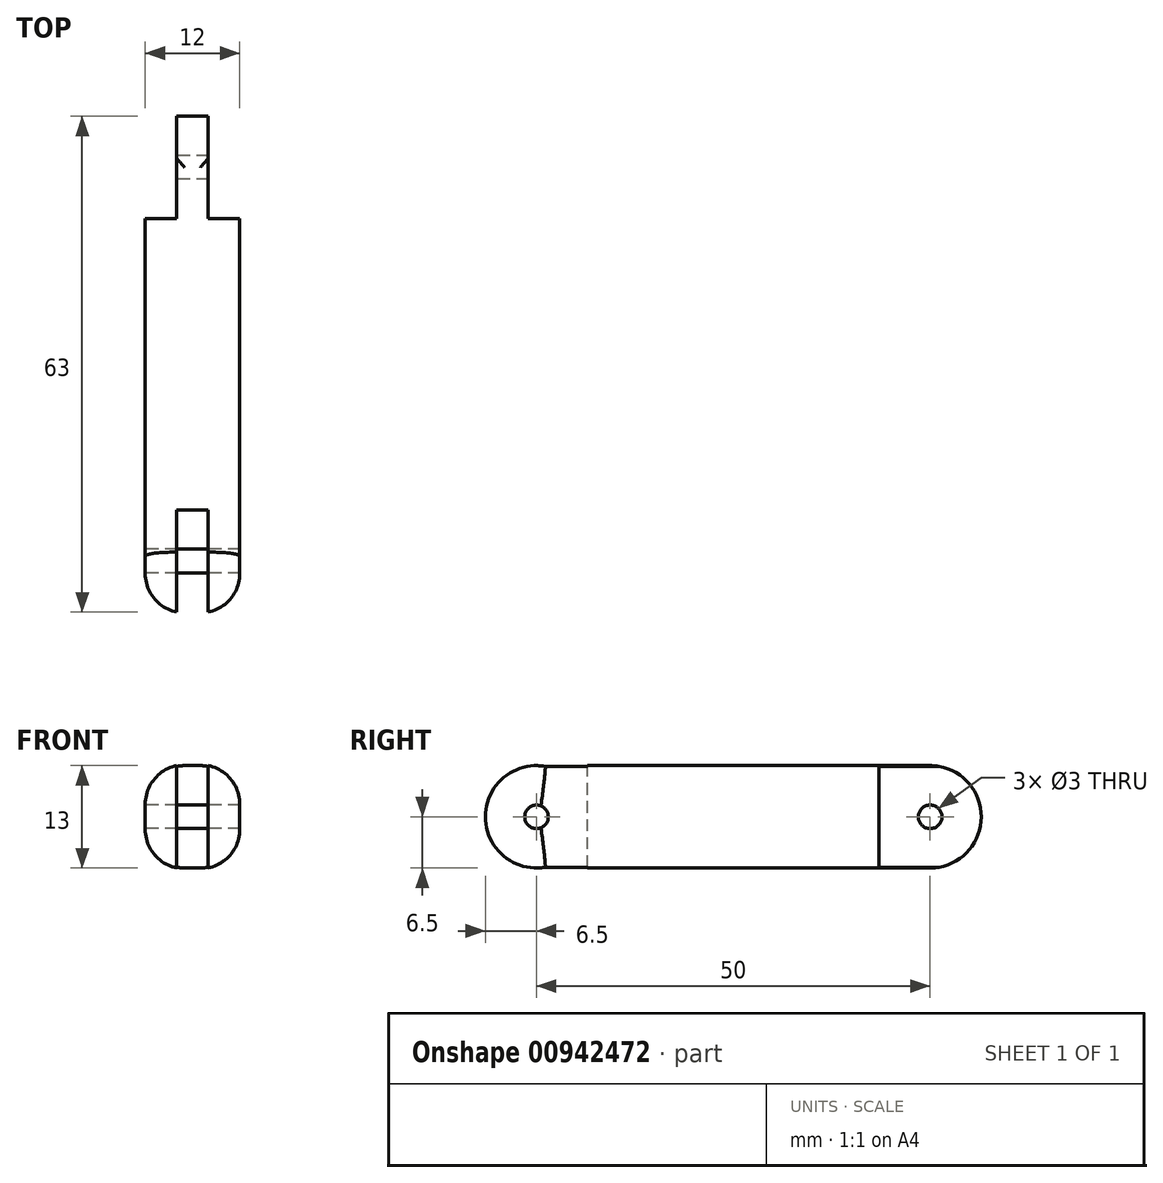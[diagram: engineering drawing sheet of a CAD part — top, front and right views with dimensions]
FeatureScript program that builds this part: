
annotation { "Feature Type Name" : "Feature", "Feature Type Description" : "" }
export const myFeature = defineFeature(function(context is Context, id is Id, definition is map)
    precondition{}
    {
        {
            var Q0;
            Q0=qCreatedBy(makeId("Right.planeOp"),FACE);
            var sketch = newSketch(context, id + "F0", { "sketchPlane" : qUnion([Q0])});
            skCircle(sketch, "E0", {"center": v(0, 0) * mm, "radius": 6.5 * mm});
            skCircle(sketch, "E1", {"center": v(0, 0) * mm, "radius": 1.5 * mm});
            skLineSegment(sketch, "E2", {"start": v(0, 6.5) * mm, "end": v(-50, 6.5) * mm});
            skLineSegment(sketch, "E3", {"start": v(0, -6.5) * mm, "end": v(-50, -6.5) * mm});
            skCircle(sketch, "E4", {"center": v(-50, 0) * mm, "radius": 6.5 * mm});
            skCircle(sketch, "E5", {"center": v(-50, 0) * mm, "radius": 1.5 * mm});
            skLineSegment(sketch, "E6", {"start": v(-43.5, 0) * mm, "end": v(-43.5, 6.5) * mm});
            skLineSegment(sketch, "E7", {"start": v(-43.5, 0) * mm, "end": v(-43.5, -6.5) * mm});
            skLineSegment(sketch, "E8", {"start": v(-6.5, 0) * mm, "end": v(-6.5, -6.5) * mm});
            skLineSegment(sketch, "E9", {"start": v(-6.5, 0) * mm, "end": v(-6.5, 6.5) * mm});
            skSolve(sketch);
        }
        {
            var Q0;
            Q0=makeQuery(id+"F0.imprint","IMPRINT",FACE,{"disambiguationData":[TD([[makeQuery(id+"F0.imprint","IMPRINT",EDGE,{"derivedFrom":sQuery(id+"F0.wireOp",EDGE,"E5")}),-1.0]])]});
            var Q1;
            {var subQ3=sQuery(id+"F0.wireOp",EDGE,"E7");Q1=makeQuery(id+"F0.imprint","IMPRINT",FACE,{"disambiguationData":[TD([[makeQuery(id+"F0.imprint","IMPRINT",EDGE,{"derivedFrom":subQ3}),-1.0]])]});}
            var Q2;
            {var subQ0=sQuery(id+"F0.wireOp",EDGE,"E6");Q2=makeQuery(id+"F0.imprint","IMPRINT",FACE,{"disambiguationData":[TD([[makeQuery(id+"F0.imprint","IMPRINT",EDGE,{"derivedFrom":subQ0}),-1.0]])]});}
            var Q3;
            {var subQ3=sQuery(id+"F0.wireOp",EDGE,"E6");Q3=makeQuery(id+"F0.imprint","IMPRINT",FACE,{"disambiguationData":[TD([[makeQuery(id+"F0.imprint","IMPRINT",EDGE,{"derivedFrom":subQ3}),1.0]])]});}
            extrude(context, id + "F1", {"entities" : qUnion([Q0, Q1, Q2, Q3]), "depth" : 12 * mm, "offsetDistance" : 25 * mm});
        }
        {
            var Q0;
            Q0=makeQuery(id+"F0.imprint","IMPRINT",FACE,{"disambiguationData":[TD([[makeQuery(id+"F0.imprint","IMPRINT",EDGE,{"derivedFrom":sQuery(id+"F0.wireOp",EDGE,"E5")}),-1.0]])]});
            var Q1;
            {var subQ3=sQuery(id+"F0.wireOp",EDGE,"E6");Q1=makeQuery(id+"F0.imprint","IMPRINT",FACE,{"disambiguationData":[TD([[makeQuery(id+"F0.imprint","IMPRINT",EDGE,{"derivedFrom":subQ3}),1.0]])]});}
            var Q2;
            {var subQ3=sQuery(id+"F0.wireOp",EDGE,"E7");Q2=makeQuery(id+"F0.imprint","IMPRINT",FACE,{"disambiguationData":[TD([[makeQuery(id+"F0.imprint","IMPRINT",EDGE,{"derivedFrom":subQ3}),-1.0]])]});}
            extrude(context, id + "F2", {"entities" : qUnion([Q0, Q1, Q2]), "operationType" : NewBodyOperationType.REMOVE, "depth" : 8 * mm, "offsetDistance" : 25 * mm, "hasSecondDirection" : true, "secondDirectionOppositeDirection" : false, "secondDirectionDepth" : 4 * mm});
        }
        {
            var Q0;
            Q0=makeQuery(id+"F0.imprint","IMPRINT",FACE,{"disambiguationData":[TD([[makeQuery(id+"F0.imprint","IMPRINT",EDGE,{"derivedFrom":sQuery(id+"F0.wireOp",EDGE,"E1")}),-1.0]])]});
            var Q1;
            {var subQ3=sQuery(id+"F0.wireOp",EDGE,"E9");Q1=makeQuery(id+"F0.imprint","IMPRINT",FACE,{"disambiguationData":[TD([[makeQuery(id+"F0.imprint","IMPRINT",EDGE,{"derivedFrom":subQ3}),-1.0]])]});}
            var Q2;
            {var subQ3=sQuery(id+"F0.wireOp",EDGE,"E8");Q2=makeQuery(id+"F0.imprint","IMPRINT",FACE,{"disambiguationData":[TD([[makeQuery(id+"F0.imprint","IMPRINT",EDGE,{"derivedFrom":subQ3}),1.0]])]});}
            extrude(context, id + "F3", {"entities" : qUnion([Q0, Q1, Q2]), "operationType" : NewBodyOperationType.ADD, "depth" : 8 * mm, "offsetDistance" : 25 * mm, "hasSecondDirection" : true, "secondDirectionOppositeDirection" : false, "secondDirectionDepth" : 4 * mm});
        }
        {
            var Q0;
            Q0=makeQuery(id+"F1.opExtrude","CAP_EDGE",EDGE,{"disambiguationData":[OSD([sQuery(id+"F0.wireOp",EDGE,"E2")])],"isStart":false});
            var Q1;
            Q1=makeQuery(id+"F1.opExtrude","CAP_EDGE",EDGE,{"disambiguationData":[OSD([sQuery(id+"F0.wireOp",EDGE,"E2")])],"isStart":true});
            fillet(context, id + "F4", {"entities" : qUnion([Q0, Q1]), "radius" : 5 * mm, "tangentPropagation" : true, "allowEdgeOverflow" : false});
        }
        {
            var Q0;
            Q0=makeQuery(id+"F0.imprint","IMPRINT",FACE,{"disambiguationData":[TD([[makeQuery(id+"F0.imprint","IMPRINT",EDGE,{"derivedFrom":sQuery(id+"F0.wireOp",EDGE,"E5")}),1.0]])]});
            extrude(context, id + "F5", {"entities" : qUnion([Q0]), "depth" : 12 * mm, "offsetDistance" : 25 * mm});
        }
    });
